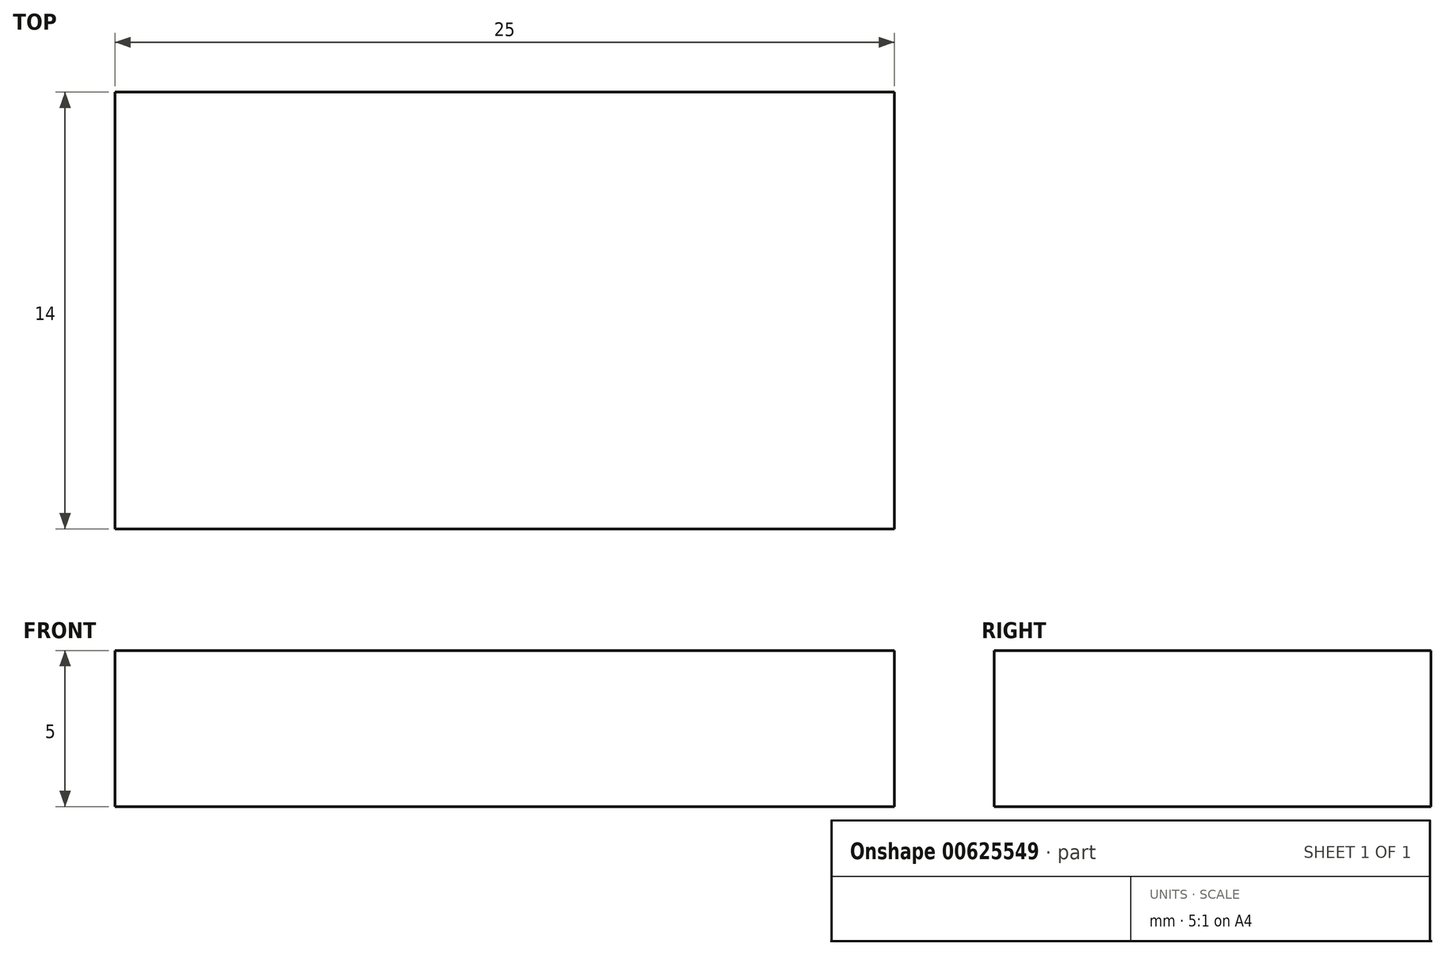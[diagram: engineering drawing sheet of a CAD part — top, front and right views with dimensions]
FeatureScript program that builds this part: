
annotation { "Feature Type Name" : "Feature", "Feature Type Description" : "" }
export const myFeature = defineFeature(function(context is Context, id is Id, definition is map)
    precondition{}
    {
        {
            var Q0;
            Q0=qCreatedBy(makeId("Top.planeOp"),FACE);
            var sketch = newSketch(context, id + "F0", { "sketchPlane" : qUnion([Q0])});
            skLineSegment(sketch, "E0.bottom", {"start": v(-12.5, 7) * mm, "end": v(12.5, 7) * mm});
            skLineSegment(sketch, "E0.top", {"start": v(-12.5, -7) * mm, "end": v(12.5, -7) * mm});
            skLineSegment(sketch, "E0.left", {"start": v(-12.5, 7) * mm, "end": v(-12.5, -7) * mm});
            skLineSegment(sketch, "E0.right", {"start": v(12.5, 7) * mm, "end": v(12.5, -7) * mm});
            skPoint(sketch, "E0.middle", {"position": v(0, 0) * mm});
            skSolve(sketch);
        }
        {
            var Q0;
            Q0 = qSketchRegion(id + "F0", true);
            extrude(context, id + "F1", {"entities" : qUnion([Q0]), "depth" : 5 * mm, "offsetDistance" : 25 * mm});
        }
    });
